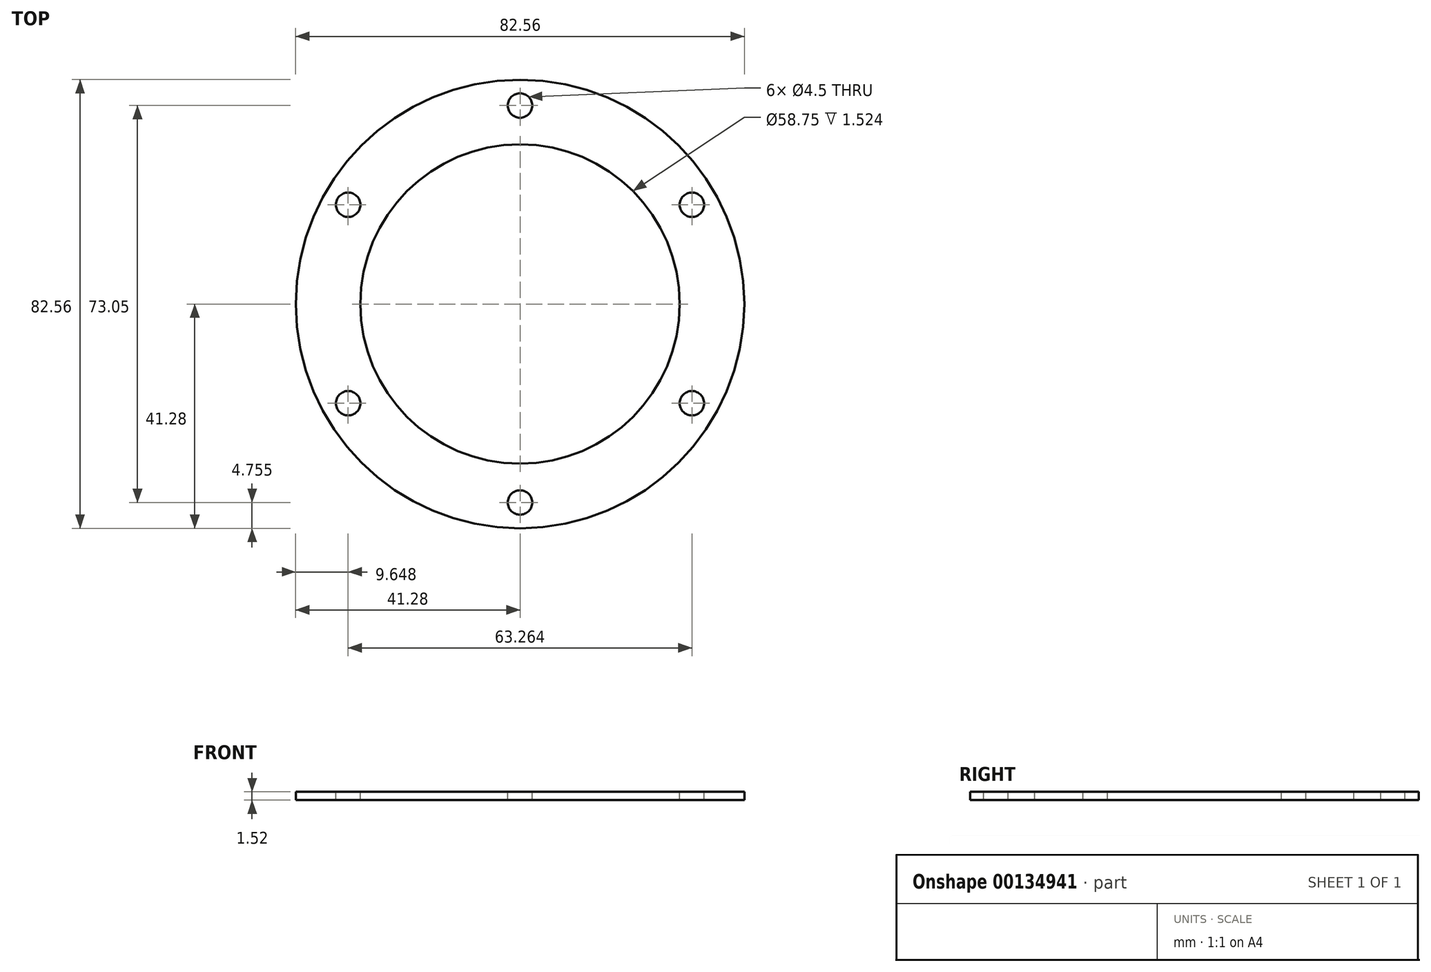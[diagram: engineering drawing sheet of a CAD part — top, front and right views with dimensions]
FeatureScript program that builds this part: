
annotation { "Feature Type Name" : "Feature", "Feature Type Description" : "" }
export const myFeature = defineFeature(function(context is Context, id is Id, definition is map)
    precondition{}
    {
        {
            var Q0;
            Q0=qCreatedBy(makeId("Top.planeOp"),FACE);
            var sketch = newSketch(context, id + "F0", { "sketchPlane" : qUnion([Q0])});
            skCircle(sketch, "E0", {"center": v(0, 0) * mm, "radius": 41.28 * mm});
            skSolve(sketch);
        }
        {
            var Q0;
            Q0 = qSketchRegion(id + "F0", true);
            extrude(context, id + "F1", {"entities" : qUnion([Q0]), "depth" : 1.52 * mm});
        }
        {
            var Q0;
            Q0=makeQuery(id+"F1.opExtrude","CAP_FACE",FACE,{"disambiguationData":[OSD([sQuery(id+"F0.wireOp",EDGE,"E0")])],"isStart":false});
            var sketch = newSketch(context, id + "F2", { "sketchPlane" : qUnion([Q0])});
            skCircle(sketch, "E1", {"center": v(0, 36.53) * mm, "radius": 2.25 * mm});
            skCircle(sketch, "E2.1.0", {"center": v(-31.63, 18.26) * mm, "radius": 2.25 * mm});
            skCircle(sketch, "E2.2.0", {"center": v(-31.63, -18.26) * mm, "radius": 2.25 * mm});
            skCircle(sketch, "E2.3.0", {"center": v(0, -36.53) * mm, "radius": 2.25 * mm});
            skCircle(sketch, "E2.4.0", {"center": v(31.63, -18.26) * mm, "radius": 2.25 * mm});
            skCircle(sketch, "E2.5.0", {"center": v(31.63, 18.26) * mm, "radius": 2.25 * mm});
            skPoint(sketch, "E2.center", {"position": v(0, 0) * mm});
            skSolve(sketch);
        }
        {
            var Q0;
            Q0 = qSketchRegion(id + "F2", true);
            extrude(context, id + "F3", {"entities" : qUnion([Q0]), "operationType" : NewBodyOperationType.REMOVE, "endBound" : BoundingType.UP_TO_NEXT, "oppositeDirection" : true, "depth" : 25.4 * mm});
        }
        {
            var Q0;
            Q0=makeQuery(id+"F1.opExtrude","CAP_FACE",FACE,{"disambiguationData":[OSD([sQuery(id+"F0.wireOp",EDGE,"E0")])],"isStart":false});
            var sketch = newSketch(context, id + "F4", { "sketchPlane" : qUnion([Q0])});
            skCircle(sketch, "E3", {"center": v(0, 0) * mm, "radius": 29.38 * mm});
            skSolve(sketch);
        }
        {
            var Q0;
            Q0 = qSketchRegion(id + "F4", true);
            extrude(context, id + "F5", {"entities" : qUnion([Q0]), "operationType" : NewBodyOperationType.REMOVE, "endBound" : BoundingType.UP_TO_NEXT, "oppositeDirection" : true, "depth" : 25.4 * mm});
        }
    });
